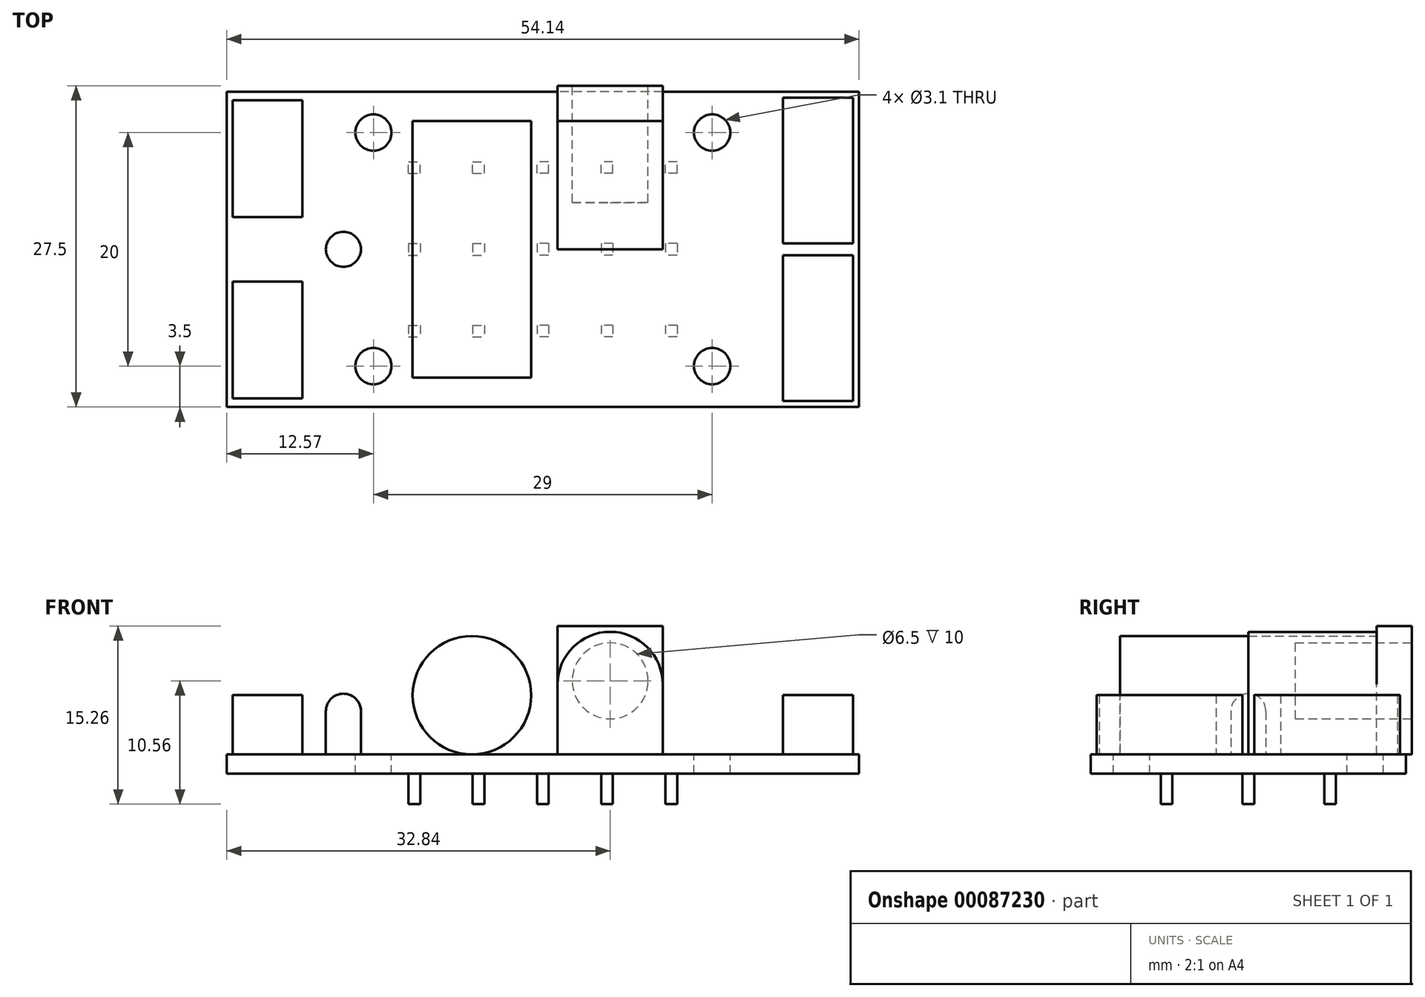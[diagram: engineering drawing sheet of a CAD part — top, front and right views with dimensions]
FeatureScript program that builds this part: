
annotation { "Feature Type Name" : "Feature", "Feature Type Description" : "" }
export const myFeature = defineFeature(function(context is Context, id is Id, definition is map)
    precondition{}
    {
        {
            var Q0;
            Q0=qCreatedBy(makeId("Top.planeOp"),FACE);
            var sketch = newSketch(context, id + "F0", { "sketchPlane" : qUnion([Q0])});
            skLineSegment(sketch, "E0.bottom", {"start": v(27.07, -13.5) * mm, "end": v(-27.07, -13.5) * mm});
            skLineSegment(sketch, "E0.top", {"start": v(27.07, 13.5) * mm, "end": v(-27.07, 13.5) * mm});
            skLineSegment(sketch, "E0.left", {"start": v(27.07, -13.5) * mm, "end": v(27.07, 13.5) * mm});
            skLineSegment(sketch, "E0.right", {"start": v(-27.07, -13.5) * mm, "end": v(-27.07, 13.5) * mm});
            skPoint(sketch, "E0.middle", {"position": v(0, 0) * mm});
            skCircle(sketch, "E1", {"center": v(-14.5, 10) * mm, "radius": 1.55 * mm});
            skCircle(sketch, "E2.MirrorC", {"center": v(14.5, 10) * mm, "radius": 1.55 * mm});
            skCircle(sketch, "E3.MirrorC", {"center": v(14.5, -10) * mm, "radius": 1.55 * mm});
            skCircle(sketch, "E4.MirrorC", {"center": v(-14.5, -10) * mm, "radius": 1.55 * mm});
            skLineSegment(sketch, "E5.bottom", {"start": v(26.57, 0.5) * mm, "end": v(20.57, 0.5) * mm});
            skLineSegment(sketch, "E5.top", {"start": v(26.57, 13) * mm, "end": v(20.57, 13) * mm});
            skLineSegment(sketch, "E5.left", {"start": v(26.57, 0.5) * mm, "end": v(26.57, 13) * mm});
            skLineSegment(sketch, "E5.right", {"start": v(20.57, 0.5) * mm, "end": v(20.57, 13) * mm});
            skPoint(sketch, "E5.middle", {"position": v(23.57, 6.75) * mm});
            skLineSegment(sketch, "E6.MirrorCS", {"start": v(26.57, -0.5) * mm, "end": v(20.57, -0.5) * mm});
            skLineSegment(sketch, "E7.MirrorCS", {"start": v(26.57, -0.5) * mm, "end": v(26.57, -13) * mm});
            skLineSegment(sketch, "E8.MirrorCS", {"start": v(20.57, -0.5) * mm, "end": v(20.57, -13) * mm});
            skLineSegment(sketch, "E9.MirrorCS", {"start": v(26.57, -13) * mm, "end": v(20.57, -13) * mm});
            skLineSegment(sketch, "E10.bottom", {"start": v(10.27, 0) * mm, "end": v(1.27, 0) * mm});
            skLineSegment(sketch, "E10.top", {"start": v(10.27, 14) * mm, "end": v(1.27, 14) * mm});
            skLineSegment(sketch, "E10.left", {"start": v(10.27, 0) * mm, "end": v(10.27, 14) * mm});
            skLineSegment(sketch, "E10.right", {"start": v(1.27, 0) * mm, "end": v(1.27, 14) * mm});
            skPoint(sketch, "E10.middle", {"position": v(5.77, 7) * mm});
            skLineSegment(sketch, "E11.bottom", {"start": v(-11.07, -11) * mm, "end": v(-1.07, -11) * mm});
            skLineSegment(sketch, "E11.top", {"start": v(-11.07, 11) * mm, "end": v(-1.07, 11) * mm});
            skLineSegment(sketch, "E11.left", {"start": v(-11.07, -11) * mm, "end": v(-11.07, 11) * mm});
            skLineSegment(sketch, "E11.right", {"start": v(-1.07, -11) * mm, "end": v(-1.07, 11) * mm});
            skPoint(sketch, "E11.middle", {"position": v(-6.07, 0) * mm});
            skCircle(sketch, "E12", {"center": v(-17.07, 0) * mm, "radius": 1.5 * mm});
            skLineSegment(sketch, "E13.bottom", {"start": v(-20.57, 2.75) * mm, "end": v(-26.57, 2.75) * mm});
            skLineSegment(sketch, "E13.top", {"start": v(-20.57, 12.75) * mm, "end": v(-26.57, 12.75) * mm});
            skLineSegment(sketch, "E13.left", {"start": v(-20.57, 2.75) * mm, "end": v(-20.57, 12.75) * mm});
            skLineSegment(sketch, "E13.right", {"start": v(-26.57, 2.75) * mm, "end": v(-26.57, 12.75) * mm});
            skPoint(sketch, "E13.middle", {"position": v(-23.57, 7.75) * mm});
            skLineSegment(sketch, "E14.MirrorCS", {"start": v(-20.57, -2.75) * mm, "end": v(-26.57, -2.75) * mm});
            skLineSegment(sketch, "E15.MirrorCS", {"start": v(-26.57, -2.75) * mm, "end": v(-26.57, -12.75) * mm});
            skLineSegment(sketch, "E16.MirrorCS", {"start": v(-20.57, -2.75) * mm, "end": v(-20.57, -12.75) * mm});
            skLineSegment(sketch, "E17.MirrorCS", {"start": v(-20.57, -12.75) * mm, "end": v(-26.57, -12.75) * mm});
            skLineSegment(sketch, "E18", {"start": v(1.27, 11) * mm, "end": v(10.27, 11) * mm});
            skSolve(sketch);
        }
        {
            var Q0;
            Q0=makeQuery(id+"F0.imprint","IMPRINT",FACE,{"disambiguationData":[TD([[makeQuery(id+"F0.imprint","IMPRINT",EDGE,{"derivedFrom":sQuery(id+"F0.wireOp",EDGE,"E13.bottom")}),-1.0]])]});
            var Q1;
            Q1=makeQuery(id+"F0.imprint","IMPRINT",FACE,{"disambiguationData":[TD([[makeQuery(id+"F0.imprint","IMPRINT",EDGE,{"derivedFrom":sQuery(id+"F0.wireOp",EDGE,"E0.bottom")}),-1.0]])]});
            var Q2;
            Q2=makeQuery(id+"F0.imprint","IMPRINT",FACE,{"disambiguationData":[TD([[makeQuery(id+"F0.imprint","IMPRINT",EDGE,{"derivedFrom":sQuery(id+"F0.wireOp",EDGE,"E14.MirrorCS")}),1.0]])]});
            var Q3;
            Q3=makeQuery(id+"F0.imprint","IMPRINT",FACE,{"disambiguationData":[TD([[makeQuery(id+"F0.imprint","IMPRINT",EDGE,{"derivedFrom":sQuery(id+"F0.wireOp",EDGE,"E11.bottom")}),1.0]])]});
            var Q4;
            {var subQ5=sQuery(id+"F0.wireOp",EDGE,"E10.bottom");Q4=makeQuery(id+"F0.imprint","IMPRINT",FACE,{"disambiguationData":[TD([[makeQuery(id+"F0.imprint","IMPRINT",EDGE,{"derivedFrom":subQ5}),-1.0]])]});}
            var Q5;
            Q5=makeQuery(id+"F0.imprint","IMPRINT",FACE,{"disambiguationData":[TD([[makeQuery(id+"F0.imprint","IMPRINT",EDGE,{"derivedFrom":sQuery(id+"F0.wireOp",EDGE,"E5.bottom")}),-1.0]])]});
            var Q6;
            Q6=makeQuery(id+"F0.imprint","IMPRINT",FACE,{"disambiguationData":[TD([[makeQuery(id+"F0.imprint","IMPRINT",EDGE,{"derivedFrom":sQuery(id+"F0.wireOp",EDGE,"E6.MirrorCS")}),1.0]])]});
            var Q7;
            Q7=makeQuery(id+"F0.imprint","IMPRINT",FACE,{"disambiguationData":[TD([[makeQuery(id+"F0.imprint","IMPRINT",EDGE,{"derivedFrom":sQuery(id+"F0.wireOp",EDGE,"E12")}),1.0]])]});
            var Q8;
            {var subQ5=sQuery(id+"F0.wireOp",EDGE,"E18");Q8=makeQuery(id+"F0.imprint","IMPRINT",FACE,{"disambiguationData":[TD([[makeQuery(id+"F0.imprint","IMPRINT",EDGE,{"derivedFrom":subQ5}),1.0]])]});}
            extrude(context, id + "F1", {"entities" : qUnion([Q0, Q1, Q2, Q3, Q4, Q5, Q6, Q7, Q8]), "oppositeDirection" : true, "depth" : 1.66 * mm});
        }
        {
            var Q0;
            {var subQ5=sQuery(id+"F0.wireOp",EDGE,"E18");Q0=makeQuery(id+"F0.imprint","IMPRINT",FACE,{"disambiguationData":[TD([[makeQuery(id+"F0.imprint","IMPRINT",EDGE,{"derivedFrom":subQ5}),1.0]])]});}
            var Q1;
            {var subQ5=sQuery(id+"F0.wireOp",EDGE,"E10.top");Q1=makeQuery(id+"F0.imprint","IMPRINT",FACE,{"disambiguationData":[TD([[makeQuery(id+"F0.imprint","IMPRINT",EDGE,{"derivedFrom":subQ5}),1.0]])]});}
            extrude(context, id + "F2", {"entities" : qUnion([Q0, Q1]), "depth" : 11 * mm});
        }
        {
            var Q0;
            {var subQ0=sQuery(id+"F0.wireOp",EDGE,"E10.bottom");Q0=makeQuery(id+"F0.imprint","IMPRINT",FACE,{"disambiguationData":[TD([[makeQuery(id+"F0.imprint","IMPRINT",EDGE,{"derivedFrom":subQ0}),-1.0]])]});}
            extrude(context, id + "F3", {"entities" : qUnion([Q0]), "operationType" : NewBodyOperationType.ADD, "depth" : 10.5 * mm});
        }
        {
            var Q0;
            Q0=makeQuery(id+"F3.opExtrude","CAP_EDGE",EDGE,{"disambiguationData":[OSD([sQuery(id+"F0.wireOp",EDGE,"E10.right")])],"isStart":false});
            var Q1;
            Q1=makeQuery(id+"F3.opExtrude","CAP_EDGE",EDGE,{"disambiguationData":[OSD([sQuery(id+"F0.wireOp",EDGE,"E10.left")])],"isStart":false});
            fillet(context, id + "F4", {"entities" : qUnion([Q0, Q1]), "radius" : 4.5 * mm, "tangentPropagation" : true, "allowEdgeOverflow" : false});
        }
        {
            var Q0;
            Q0=makeQuery(id+"F2.opExtrude","SWEPT_FACE",FACE,{"disambiguationData":[OSD([sQuery(id+"F0.wireOp",EDGE,"E10.top")])]});
            var sketch = newSketch(context, id + "F5", { "sketchPlane" : qUnion([Q0])});
            skCircle(sketch, "E19", {"center": v(-5.77, 6.3) * mm, "radius": 3.25 * mm});
            skPoint(sketch, "E19.centerSnap0", {"position": v(-5.77, 0) * mm});
            skSolve(sketch);
        }
        {
            var Q0;
            Q0=makeQuery(id+"F5.imprint","IMPRINT",FACE,{"disambiguationData":[TD([[makeQuery(id+"F5.imprint","IMPRINT",EDGE,{"derivedFrom":sQuery(id+"F5.wireOp",EDGE,"E19")}),1.0]])]});
            extrude(context, id + "F6", {"entities" : qUnion([Q0]), "operationType" : NewBodyOperationType.REMOVE, "oppositeDirection" : true, "depth" : 10 * mm});
        }
        {
            var Q0;
            Q0=makeQuery(id+"F0.imprint","IMPRINT",FACE,{"disambiguationData":[TD([[makeQuery(id+"F0.imprint","IMPRINT",EDGE,{"derivedFrom":sQuery(id+"F0.wireOp",EDGE,"E12")}),1.0]])]});
            extrude(context, id + "F7", {"entities" : qUnion([Q0]), "depth" : 5.2 * mm});
        }
        {
            var Q0;
            Q0=makeQuery(id+"F7.opExtrude","CAP_EDGE",EDGE,{"disambiguationData":[OSD([sQuery(id+"F0.wireOp",EDGE,"E12")])],"isStart":false});
            fillet(context, id + "F8", {"entities" : qUnion([Q0]), "radius" : 1.5 * mm, "tangentPropagation" : true, "allowEdgeOverflow" : false});
        }
        {
            var Q0;
            Q0=qCreatedBy(makeId("Front.planeOp"),FACE);
            var sketch = newSketch(context, id + "F9", { "sketchPlane" : qUnion([Q0])});
            skCircle(sketch, "E20", {"center": v(-6.07, 5.07) * mm, "radius": 5.07 * mm});
            skSolve(sketch);
        }
        {
            var Q0;
            Q0=makeQuery(id+"F9.imprint","IMPRINT",FACE,{"disambiguationData":[TD([[makeQuery(id+"F9.imprint","IMPRINT",EDGE,{"derivedFrom":sQuery(id+"F9.wireOp",EDGE,"E20")}),1.0]])]});
            extrude(context, id + "F10", {"entities" : qUnion([Q0]), "depth" : 11 * mm, "hasSecondDirection" : true, "secondDirectionOppositeDirection" : true, "secondDirectionDepth" : 11 * mm});
        }
        {
            var Q0;
            Q0=makeQuery(id+"F0.imprint","IMPRINT",FACE,{"disambiguationData":[TD([[makeQuery(id+"F0.imprint","IMPRINT",EDGE,{"derivedFrom":sQuery(id+"F0.wireOp",EDGE,"E5.bottom")}),-1.0]])]});
            var Q1;
            Q1=makeQuery(id+"F0.imprint","IMPRINT",FACE,{"disambiguationData":[TD([[makeQuery(id+"F0.imprint","IMPRINT",EDGE,{"derivedFrom":sQuery(id+"F0.wireOp",EDGE,"E6.MirrorCS")}),1.0]])]});
            var Q2;
            Q2=makeQuery(id+"F0.imprint","IMPRINT",FACE,{"disambiguationData":[TD([[makeQuery(id+"F0.imprint","IMPRINT",EDGE,{"derivedFrom":sQuery(id+"F0.wireOp",EDGE,"E14.MirrorCS")}),1.0]])]});
            var Q3;
            Q3=makeQuery(id+"F0.imprint","IMPRINT",FACE,{"disambiguationData":[TD([[makeQuery(id+"F0.imprint","IMPRINT",EDGE,{"derivedFrom":sQuery(id+"F0.wireOp",EDGE,"E13.bottom")}),-1.0]])]});
            extrude(context, id + "F11", {"entities" : qUnion([Q0, Q1, Q2, Q3]), "depth" : 5.1 * mm});
        }
        {
            var Q0;
            Q0=makeQuery(id+"F1.opExtrude","CAP_FACE",FACE,{"disambiguationData":[OSD([sQuery(id+"F0.wireOp",EDGE,"E0.bottom"),sQuery(id+"F0.wireOp",EDGE,"E0.top"),sQuery(id+"F0.wireOp",EDGE,"E0.left"),sQuery(id+"F0.wireOp",EDGE,"E0.right"),sQuery(id+"F0.wireOp",EDGE,"E1"),sQuery(id+"F0.wireOp",EDGE,"E2.MirrorC"),sQuery(id+"F0.wireOp",EDGE,"E3.MirrorC"),sQuery(id+"F0.wireOp",EDGE,"E4.MirrorC")])],"isStart":false});
            var sketch = newSketch(context, id + "F12", { "sketchPlane" : qUnion([Q0])});
            skLineSegment(sketch, "E21.bottom", {"start": v(0.5, -0.5) * mm, "end": v(-0.5, -0.5) * mm});
            skLineSegment(sketch, "E21.top", {"start": v(0.5, 0.5) * mm, "end": v(-0.5, 0.5) * mm});
            skLineSegment(sketch, "E21.left", {"start": v(0.5, -0.5) * mm, "end": v(0.5, 0.5) * mm});
            skLineSegment(sketch, "E21.right", {"start": v(-0.5, -0.5) * mm, "end": v(-0.5, 0.5) * mm});
            skPoint(sketch, "E21.middle", {"position": v(0, 0) * mm});
            skLineSegment(sketch, "E22.0.1.0", {"start": v(0.5, 6.5) * mm, "end": v(0.5, 7.5) * mm});
            skLineSegment(sketch, "E22.0.1.1", {"start": v(0.5, 7.5) * mm, "end": v(-0.5, 7.5) * mm});
            skLineSegment(sketch, "E22.0.1.2", {"start": v(-0.5, 6.5) * mm, "end": v(-0.5, 7.5) * mm});
            skLineSegment(sketch, "E22.0.1.3", {"start": v(0.5, 6.5) * mm, "end": v(-0.5, 6.5) * mm});
            skLineSegment(sketch, "E22.1.0.0", {"start": v(6, -0.5) * mm, "end": v(6, 0.5) * mm});
            skLineSegment(sketch, "E22.1.0.1", {"start": v(6, 0.5) * mm, "end": v(5, 0.5) * mm});
            skLineSegment(sketch, "E22.1.0.2", {"start": v(5, -0.5) * mm, "end": v(5, 0.5) * mm});
            skLineSegment(sketch, "E22.1.0.3", {"start": v(6, -0.5) * mm, "end": v(5, -0.5) * mm});
            skLineSegment(sketch, "E22.1.1.0", {"start": v(6, 6.5) * mm, "end": v(6, 7.5) * mm});
            skLineSegment(sketch, "E22.1.1.1", {"start": v(6, 7.5) * mm, "end": v(5, 7.5) * mm});
            skLineSegment(sketch, "E22.1.1.2", {"start": v(5, 6.5) * mm, "end": v(5, 7.5) * mm});
            skLineSegment(sketch, "E22.1.1.3", {"start": v(6, 6.5) * mm, "end": v(5, 6.5) * mm});
            skLineSegment(sketch, "E22.2.0.0", {"start": v(11.5, -0.5) * mm, "end": v(11.5, 0.5) * mm});
            skLineSegment(sketch, "E22.2.0.1", {"start": v(11.5, 0.5) * mm, "end": v(10.5, 0.5) * mm});
            skLineSegment(sketch, "E22.2.0.2", {"start": v(10.5, -0.5) * mm, "end": v(10.5, 0.5) * mm});
            skLineSegment(sketch, "E22.2.0.3", {"start": v(11.5, -0.5) * mm, "end": v(10.5, -0.5) * mm});
            skLineSegment(sketch, "E22.2.1.0", {"start": v(11.5, 6.5) * mm, "end": v(11.5, 7.5) * mm});
            skLineSegment(sketch, "E22.2.1.1", {"start": v(11.5, 7.5) * mm, "end": v(10.5, 7.5) * mm});
            skLineSegment(sketch, "E22.2.1.2", {"start": v(10.5, 6.5) * mm, "end": v(10.5, 7.5) * mm});
            skLineSegment(sketch, "E22.2.1.3", {"start": v(11.5, 6.5) * mm, "end": v(10.5, 6.5) * mm});
            skLineSegment(sketch, "E22.direction1", {"start": v(0.5, -0.5) * mm, "end": v(6, -0.5) * mm, "construction": true});
            skLineSegment(sketch, "E22.direction2", {"start": v(0.5, -0.5) * mm, "end": v(0.5, 6.5) * mm, "construction": true});
            skLineSegment(sketch, "E23.MirrorCS", {"start": v(11.5, -6.5) * mm, "end": v(10.5, -6.5) * mm});
            skLineSegment(sketch, "E24.MirrorCS", {"start": v(11.5, -6.5) * mm, "end": v(11.5, -7.5) * mm});
            skLineSegment(sketch, "E25.MirrorCS", {"start": v(11.5, -7.5) * mm, "end": v(10.5, -7.5) * mm});
            skLineSegment(sketch, "E26.MirrorCS", {"start": v(10.5, -6.5) * mm, "end": v(10.5, -7.5) * mm});
            skLineSegment(sketch, "E27.MirrorCS", {"start": v(6, -6.5) * mm, "end": v(5, -6.5) * mm});
            skLineSegment(sketch, "E28.MirrorCS", {"start": v(6, -6.5) * mm, "end": v(6, -7.5) * mm});
            skLineSegment(sketch, "E29.MirrorCS", {"start": v(6, -7.5) * mm, "end": v(5, -7.5) * mm});
            skLineSegment(sketch, "E30.MirrorCS", {"start": v(5, -6.5) * mm, "end": v(5, -7.5) * mm});
            skLineSegment(sketch, "E31.MirrorCS", {"start": v(0.5, -6.5) * mm, "end": v(-0.5, -6.5) * mm});
            skLineSegment(sketch, "E32.MirrorCS", {"start": v(-0.5, -6.5) * mm, "end": v(-0.5, -7.5) * mm});
            skLineSegment(sketch, "E33.MirrorCS", {"start": v(0.5, -6.5) * mm, "end": v(0.5, -7.5) * mm});
            skLineSegment(sketch, "E34.MirrorCS", {"start": v(0.5, -7.5) * mm, "end": v(-0.5, -7.5) * mm});
            skLineSegment(sketch, "E35.MirrorCS", {"start": v(-6, -6.5) * mm, "end": v(-6, -7.5) * mm});
            skLineSegment(sketch, "E36.MirrorCS", {"start": v(-10.5, 6.5) * mm, "end": v(-10.5, 7.5) * mm});
            skLineSegment(sketch, "E37.MirrorCS", {"start": v(-11.5, -0.5) * mm, "end": v(-10.5, -0.5) * mm});
            skLineSegment(sketch, "E38.MirrorCS", {"start": v(-11.5, -6.5) * mm, "end": v(-10.5, -6.5) * mm});
            skLineSegment(sketch, "E39.MirrorCS", {"start": v(-10.5, -0.5) * mm, "end": v(-10.5, 0.5) * mm});
            skLineSegment(sketch, "E40.MirrorCS", {"start": v(-0.5, -0.5) * mm, "end": v(-6, -0.5) * mm, "construction": true});
            skLineSegment(sketch, "E41.MirrorCS", {"start": v(-11.5, 7.5) * mm, "end": v(-10.5, 7.5) * mm});
            skLineSegment(sketch, "E42.MirrorCS", {"start": v(-6, -6.5) * mm, "end": v(-5, -6.5) * mm});
            skLineSegment(sketch, "E43.MirrorCS", {"start": v(-11.5, -6.5) * mm, "end": v(-11.5, -7.5) * mm});
            skLineSegment(sketch, "E44.MirrorCS", {"start": v(-11.5, -0.5) * mm, "end": v(-11.5, 0.5) * mm});
            skLineSegment(sketch, "E45.MirrorCS", {"start": v(-6, -7.5) * mm, "end": v(-5, -7.5) * mm});
            skLineSegment(sketch, "E46.MirrorCS", {"start": v(-5, 6.5) * mm, "end": v(-5, 7.5) * mm});
            skLineSegment(sketch, "E47.MirrorCS", {"start": v(-6, 6.5) * mm, "end": v(-5, 6.5) * mm});
            skLineSegment(sketch, "E48.MirrorCS", {"start": v(-11.5, -7.5) * mm, "end": v(-10.5, -7.5) * mm});
            skLineSegment(sketch, "E49.MirrorCS", {"start": v(-11.5, 0.5) * mm, "end": v(-10.5, 0.5) * mm});
            skLineSegment(sketch, "E50.MirrorCS", {"start": v(-5, -6.5) * mm, "end": v(-5, -7.5) * mm});
            skLineSegment(sketch, "E51.MirrorCS", {"start": v(-11.5, 6.5) * mm, "end": v(-10.5, 6.5) * mm});
            skLineSegment(sketch, "E52.MirrorCS", {"start": v(-6, 7.5) * mm, "end": v(-5, 7.5) * mm});
            skLineSegment(sketch, "E53.MirrorCS", {"start": v(-6, 6.5) * mm, "end": v(-6, 7.5) * mm});
            skLineSegment(sketch, "E54.MirrorCS", {"start": v(-6, -0.5) * mm, "end": v(-5, -0.5) * mm});
            skLineSegment(sketch, "E55.MirrorCS", {"start": v(-5, -0.5) * mm, "end": v(-5, 0.5) * mm});
            skLineSegment(sketch, "E56.MirrorCS", {"start": v(-11.5, 6.5) * mm, "end": v(-11.5, 7.5) * mm});
            skLineSegment(sketch, "E57.MirrorCS", {"start": v(-6, 0.5) * mm, "end": v(-5, 0.5) * mm});
            skLineSegment(sketch, "E58.MirrorCS", {"start": v(-10.5, -6.5) * mm, "end": v(-10.5, -7.5) * mm});
            skLineSegment(sketch, "E59.MirrorCS", {"start": v(-6, -0.5) * mm, "end": v(-6, 0.5) * mm});
            skSolve(sketch);
        }
        {
            var Q0;
            Q0=makeQuery(id+"F12.imprint","IMPRINT",FACE,{"disambiguationData":[TD([[makeQuery(id+"F12.imprint","IMPRINT",EDGE,{"derivedFrom":sQuery(id+"F12.wireOp",EDGE,"E21.bottom")}),-1.0]])]});
            var Q1;
            Q1=makeQuery(id+"F12.imprint","IMPRINT",FACE,{"disambiguationData":[TD([[makeQuery(id+"F12.imprint","IMPRINT",EDGE,{"derivedFrom":sQuery(id+"F12.wireOp",EDGE,"E22.0.1.0")}),1.0]])]});
            var Q2;
            Q2=makeQuery(id+"F12.imprint","IMPRINT",FACE,{"disambiguationData":[TD([[makeQuery(id+"F12.imprint","IMPRINT",EDGE,{"derivedFrom":sQuery(id+"F12.wireOp",EDGE,"E22.1.1.0")}),1.0]])]});
            var Q3;
            Q3=makeQuery(id+"F12.imprint","IMPRINT",FACE,{"disambiguationData":[TD([[makeQuery(id+"F12.imprint","IMPRINT",EDGE,{"derivedFrom":sQuery(id+"F12.wireOp",EDGE,"E22.2.1.0")}),1.0]])]});
            var Q4;
            Q4=makeQuery(id+"F12.imprint","IMPRINT",FACE,{"disambiguationData":[TD([[makeQuery(id+"F12.imprint","IMPRINT",EDGE,{"derivedFrom":sQuery(id+"F12.wireOp",EDGE,"E22.2.0.0")}),1.0]])]});
            var Q5;
            Q5=makeQuery(id+"F12.imprint","IMPRINT",FACE,{"disambiguationData":[TD([[makeQuery(id+"F12.imprint","IMPRINT",EDGE,{"derivedFrom":sQuery(id+"F12.wireOp",EDGE,"E22.1.0.0")}),1.0]])]});
            var Q6;
            Q6=makeQuery(id+"F12.imprint","IMPRINT",FACE,{"disambiguationData":[TD([[makeQuery(id+"F12.imprint","IMPRINT",EDGE,{"derivedFrom":sQuery(id+"F12.wireOp",EDGE,"E23.MirrorCS")}),1.0]])]});
            var Q7;
            Q7=makeQuery(id+"F12.imprint","IMPRINT",FACE,{"disambiguationData":[TD([[makeQuery(id+"F12.imprint","IMPRINT",EDGE,{"derivedFrom":sQuery(id+"F12.wireOp",EDGE,"E27.MirrorCS")}),1.0]])]});
            var Q8;
            Q8=makeQuery(id+"F12.imprint","IMPRINT",FACE,{"disambiguationData":[TD([[makeQuery(id+"F12.imprint","IMPRINT",EDGE,{"derivedFrom":sQuery(id+"F12.wireOp",EDGE,"E31.MirrorCS")}),1.0]])]});
            var Q9;
            Q9=makeQuery(id+"F12.imprint","IMPRINT",FACE,{"disambiguationData":[TD([[makeQuery(id+"F12.imprint","IMPRINT",EDGE,{"derivedFrom":sQuery(id+"F12.wireOp",EDGE,"E35.MirrorCS")}),1.0]])]});
            var Q10;
            Q10=makeQuery(id+"F12.imprint","IMPRINT",FACE,{"disambiguationData":[TD([[makeQuery(id+"F12.imprint","IMPRINT",EDGE,{"derivedFrom":sQuery(id+"F12.wireOp",EDGE,"E54.MirrorCS")}),1.0]])]});
            var Q11;
            Q11=makeQuery(id+"F12.imprint","IMPRINT",FACE,{"disambiguationData":[TD([[makeQuery(id+"F12.imprint","IMPRINT",EDGE,{"derivedFrom":sQuery(id+"F12.wireOp",EDGE,"E47.MirrorCS")}),1.0]])]});
            var Q12;
            Q12=makeQuery(id+"F12.imprint","IMPRINT",FACE,{"disambiguationData":[TD([[makeQuery(id+"F12.imprint","IMPRINT",EDGE,{"derivedFrom":sQuery(id+"F12.wireOp",EDGE,"E36.MirrorCS")}),1.0]])]});
            var Q13;
            Q13=makeQuery(id+"F12.imprint","IMPRINT",FACE,{"disambiguationData":[TD([[makeQuery(id+"F12.imprint","IMPRINT",EDGE,{"derivedFrom":sQuery(id+"F12.wireOp",EDGE,"E37.MirrorCS")}),1.0]])]});
            var Q14;
            Q14=makeQuery(id+"F12.imprint","IMPRINT",FACE,{"disambiguationData":[TD([[makeQuery(id+"F12.imprint","IMPRINT",EDGE,{"derivedFrom":sQuery(id+"F12.wireOp",EDGE,"E38.MirrorCS")}),-1.0]])]});
            extrude(context, id + "F13", {"entities" : qUnion([Q0, Q1, Q2, Q3, Q4, Q5, Q6, Q7, Q8, Q9, Q10, Q11, Q12, Q13, Q14]), "operationType" : NewBodyOperationType.ADD, "depth" : 2.6 * mm});
        }
    });
